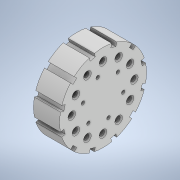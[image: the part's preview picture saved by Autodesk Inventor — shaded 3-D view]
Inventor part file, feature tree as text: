
AUTODESK INVENTOR PART (.ipt)
format: ipt  version: 2022 (Build 260153000, 153)  size: 273,408 bytes
history: native  units: mm
features: sketch x4, hole x2, chamfer x2, other x1, revolve x1, extrude x1
ambient origin geometry x8: Origin, YZ Plane, XZ Plane, XY Plane, X Axis, Y Axis, Z Axis, Center Point
bodies: Body1 (feature_tree)
feature tree (11):
  other  "Твердое тело1"
  revolve  "Вращение1"
  extrude  "Выдавливание1"  Depth=15.0mm
  hole  "Отверстие1"  [1 undecoded]
  chamfer  "Фаска1"  Angle=90.0deg  [1 undecoded]
  chamfer  "Фаска2"  Distance=3.0mm
  hole  "Отверстие2"  [1 undecoded]
  sketch  "Эскиз1"
  sketch  "Эскиз2"
  sketch  "Эскиз3"
  sketch  "Эскиз4"
note: 3 required parameter values undecoded (feature->parameter linkage not recoverable at this tier; creation-order binding heuristic only, values carry confidence <= 0.55)
